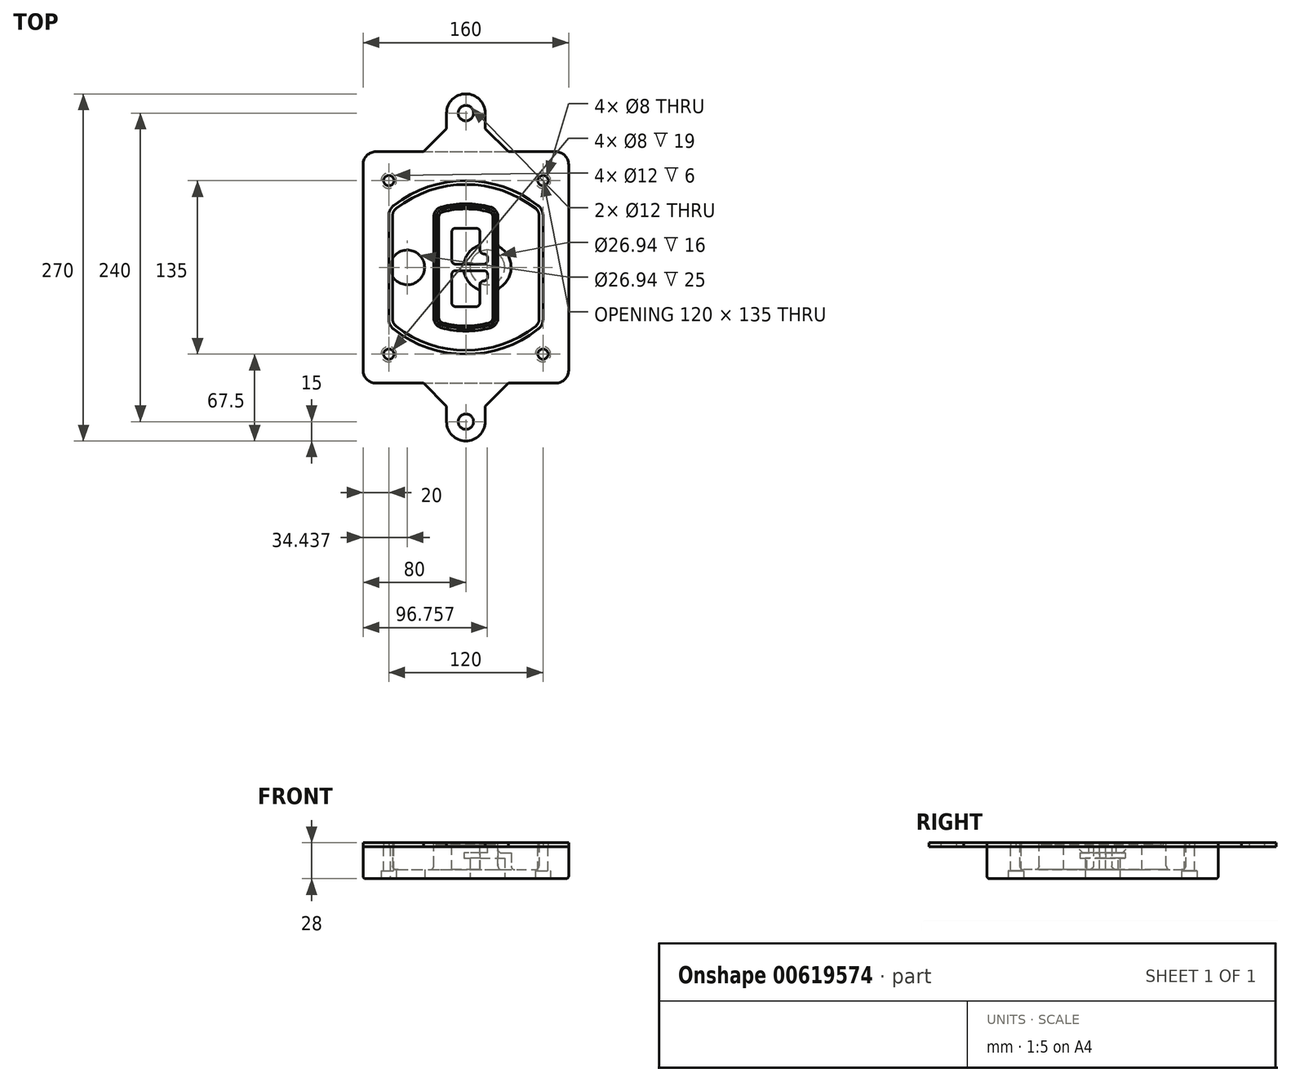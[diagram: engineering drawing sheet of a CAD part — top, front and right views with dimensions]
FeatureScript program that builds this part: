
annotation { "Feature Type Name" : "Feature", "Feature Type Description" : "" }
export const myFeature = defineFeature(function(context is Context, id is Id, definition is map)
    precondition{}
    {
        {
            var Q0;
            Q0=qCreatedBy(makeId("Top.planeOp"),FACE);
            var sketch = newSketch(context, id + "F0", { "sketchPlane" : qUnion([Q0])});
            skPoint(sketch, "E0.rect.middle", {"position": v(0, 0) * mm});
            skLineSegment(sketch, "E1.bottom", {"start": v(-70, -90) * mm, "end": v(70, -90) * mm});
            skLineSegment(sketch, "E1.top", {"start": v(-70, 90) * mm, "end": v(70, 90) * mm});
            skLineSegment(sketch, "E1.left", {"start": v(-80, -80) * mm, "end": v(-80, 80) * mm});
            skLineSegment(sketch, "E1.right", {"start": v(80, -80) * mm, "end": v(80, 80) * mm});
            skLineSegment(sketch, "E2", {"start": v(-80, 90) * mm, "end": v(80, -90) * mm, "construction": true});
            skLineSegment(sketch, "E3", {"start": v(80, 90) * mm, "end": v(-80, -90) * mm, "construction": true});
            skCircle(sketch, "E4", {"center": v(-60, 67.5) * mm, "radius": 4 * mm});
            skCircle(sketch, "E5", {"center": v(60, 67.5) * mm, "radius": 4 * mm});
            skCircle(sketch, "E6", {"center": v(60, -67.5) * mm, "radius": 4 * mm});
            skCircle(sketch, "E7", {"center": v(-60, -67.5) * mm, "radius": 4 * mm});
            skLineSegment(sketch, "E8", {"start": v(-60, 67.5) * mm, "end": v(60, 67.5) * mm, "construction": true});
            skLineSegment(sketch, "E9", {"start": v(60, 67.5) * mm, "end": v(60, -67.5) * mm, "construction": true});
            skLineSegment(sketch, "E10", {"start": v(60, -67.5) * mm, "end": v(-60, -67.5) * mm, "construction": true});
            skLineSegment(sketch, "E11", {"start": v(-60, -67.5) * mm, "end": v(-60, 67.5) * mm, "construction": true});
            skLineSegment(sketch, "E12", {"start": v(-60, 40.3) * mm, "end": v(-60, -40.3) * mm});
            skLineSegment(sketch, "E13", {"start": v(60, 40.3) * mm, "end": v(60, -40.3) * mm});
            skArc(sketch, "E14", {"start": v(56.15, 48.18) * mm, "mid": v(0, 67.5) * mm, "end": v(-56.15, 48.18) * mm});
            skArc(sketch, "E15", {"start": v(-56.15, -48.18) * mm, "mid": v(0, -67.5) * mm, "end": v(56.15, -48.18) * mm});
            skLineSegment(sketch, "E16", {"start": v(-60, 0) * mm, "end": v(60, 0) * mm, "construction": true});
            skPoint(sketch, "E17.visualSharp", {"position": v(-60, -45) * mm});
            skArc(sketch, "E17.filletArc", {"start": v(-60, -40.3) * mm, "mid": v(-58.99, -44.68) * mm, "end": v(-56.15, -48.18) * mm});
            skPoint(sketch, "E18.visualSharp", {"position": v(-60, 45) * mm});
            skArc(sketch, "E18.filletArc", {"start": v(-56.15, 48.18) * mm, "mid": v(-58.99, 44.68) * mm, "end": v(-60, 40.3) * mm});
            skPoint(sketch, "E19.visualSharp", {"position": v(60, 45) * mm});
            skArc(sketch, "E19.filletArc", {"start": v(60, 40.3) * mm, "mid": v(58.99, 44.68) * mm, "end": v(56.15, 48.18) * mm});
            skPoint(sketch, "E20.visualSharp", {"position": v(60, -45) * mm});
            skArc(sketch, "E20.filletArc", {"start": v(56.15, -48.18) * mm, "mid": v(58.99, -44.68) * mm, "end": v(60, -40.3) * mm});
            skPoint(sketch, "E21.visualSharp", {"position": v(-80, 90) * mm});
            skArc(sketch, "E21.filletArc", {"start": v(-70, 90) * mm, "mid": v(-77.07, 87.07) * mm, "end": v(-80, 80) * mm});
            skPoint(sketch, "E22.visualSharp", {"position": v(80, 90) * mm});
            skArc(sketch, "E22.filletArc", {"start": v(80, 80) * mm, "mid": v(77.07, 87.07) * mm, "end": v(70, 90) * mm});
            skPoint(sketch, "E23.visualSharp", {"position": v(80, -90) * mm});
            skArc(sketch, "E23.filletArc", {"start": v(70, -90) * mm, "mid": v(77.07, -87.07) * mm, "end": v(80, -80) * mm});
            skPoint(sketch, "E24.visualSharp", {"position": v(-80, -90) * mm});
            skArc(sketch, "E24.filletArc", {"start": v(-80, -80) * mm, "mid": v(-77.07, -87.07) * mm, "end": v(-70, -90) * mm});
            skArc(sketch, "E25.0", {"start": v(57, 40.3) * mm, "mid": v(56.3, 43.36) * mm, "end": v(54.3, 45.81) * mm});
            skLineSegment(sketch, "E25.1", {"start": v(57, 40.3) * mm, "end": v(57, -40.3) * mm});
            skArc(sketch, "E25.2", {"start": v(54.3, -45.81) * mm, "mid": v(56.3, -43.36) * mm, "end": v(57, -40.3) * mm});
            skArc(sketch, "E25.3", {"start": v(-54.3, -45.81) * mm, "mid": v(0, -64.5) * mm, "end": v(54.3, -45.81) * mm});
            skArc(sketch, "E25.4", {"start": v(-57, -40.3) * mm, "mid": v(-56.3, -43.36) * mm, "end": v(-54.3, -45.81) * mm});
            skArc(sketch, "E25.5", {"start": v(54.3, 45.81) * mm, "mid": v(0, 64.5) * mm, "end": v(-54.3, 45.81) * mm});
            skLineSegment(sketch, "E25.6", {"start": v(-57, 40.3) * mm, "end": v(-57, -40.3) * mm});
            skArc(sketch, "E25.7", {"start": v(-54.3, 45.81) * mm, "mid": v(-56.3, 43.36) * mm, "end": v(-57, 40.3) * mm});
            skArc(sketch, "E26.0", {"start": v(-58.62, 51.33) * mm, "mid": v(-62.58, 46.43) * mm, "end": v(-64, 40.3) * mm});
            skArc(sketch, "E26.1", {"start": v(58.62, 51.33) * mm, "mid": v(0, 71.5) * mm, "end": v(-58.62, 51.33) * mm});
            skArc(sketch, "E26.2", {"start": v(64, 40.3) * mm, "mid": v(62.58, 46.43) * mm, "end": v(58.62, 51.33) * mm});
            skLineSegment(sketch, "E26.3", {"start": v(64, 40.3) * mm, "end": v(64, -40.3) * mm});
            skArc(sketch, "E26.4", {"start": v(58.62, -51.33) * mm, "mid": v(62.58, -46.43) * mm, "end": v(64, -40.3) * mm});
            skLineSegment(sketch, "E26.5", {"start": v(-64, 40.3) * mm, "end": v(-64, -40.3) * mm});
            skArc(sketch, "E26.6", {"start": v(-58.62, -51.33) * mm, "mid": v(0, -71.5) * mm, "end": v(58.62, -51.33) * mm});
            skArc(sketch, "E26.7", {"start": v(-64, -40.3) * mm, "mid": v(-62.58, -46.43) * mm, "end": v(-58.62, -51.33) * mm});
            skSolve(sketch);
        }
        {
            var Q0;
            Q0=makeQuery(id+"F0.imprint","IMPRINT",FACE,{"disambiguationData":[TD([[makeQuery(id+"F0.imprint","IMPRINT",EDGE,{"derivedFrom":sQuery(id+"F0.wireOp",EDGE,"E1.bottom")}),1.0]])]});
            var Q1;
            Q1=makeQuery(id+"F0.imprint","IMPRINT",FACE,{"disambiguationData":[TD([[makeQuery(id+"F0.imprint","IMPRINT",EDGE,{"derivedFrom":sQuery(id+"F0.wireOp",EDGE,"E12")}),1.0]])]});
            var Q2;
            Q2=makeQuery(id+"F0.imprint","IMPRINT",FACE,{"disambiguationData":[TD([[makeQuery(id+"F0.imprint","IMPRINT",EDGE,{"derivedFrom":sQuery(id+"F0.wireOp",EDGE,"E25.0")}),1.0]])]});
            var Q3;
            Q3=makeQuery(id+"F0.imprint","IMPRINT",FACE,{"disambiguationData":[TD([[makeQuery(id+"F0.imprint","IMPRINT",EDGE,{"derivedFrom":sQuery(id+"F0.wireOp",EDGE,"E12")}),-1.0]])]});
            extrude(context, id + "F1", {"entities" : qUnion([Q0, Q1, Q2, Q3]), "oppositeDirection" : true, "depth" : 25 * mm});
        }
        {
            var Q0;
            Q0=makeQuery(id+"F0.imprint","IMPRINT",FACE,{"disambiguationData":[TD([[makeQuery(id+"F0.imprint","IMPRINT",EDGE,{"derivedFrom":sQuery(id+"F0.wireOp",EDGE,"E12")}),1.0]])]});
            extrude(context, id + "F2", {"entities" : qUnion([Q0]), "operationType" : NewBodyOperationType.ADD, "depth" : 3 * mm});
        }
        {
            var Q0;
            Q0=makeQuery(id+"F0.imprint","IMPRINT",FACE,{"disambiguationData":[TD([[makeQuery(id+"F0.imprint","IMPRINT",EDGE,{"derivedFrom":sQuery(id+"F0.wireOp",EDGE,"E25.0")}),1.0]])]});
            extrude(context, id + "F3", {"entities" : qUnion([Q0]), "operationType" : NewBodyOperationType.REMOVE, "oppositeDirection" : true, "depth" : 18 * mm});
        }
        {
            var Q0;
            Q0=makeQuery(id+"F2.opExtrude","CAP_FACE",FACE,{"disambiguationData":[OSD([sQuery(id+"F0.wireOp",EDGE,"E12"),sQuery(id+"F0.wireOp",EDGE,"E13"),sQuery(id+"F0.wireOp",EDGE,"E14"),sQuery(id+"F0.wireOp",EDGE,"E15"),sQuery(id+"F0.wireOp",EDGE,"E17.filletArc"),sQuery(id+"F0.wireOp",EDGE,"E18.filletArc"),sQuery(id+"F0.wireOp",EDGE,"E19.filletArc"),sQuery(id+"F0.wireOp",EDGE,"E20.filletArc"),sQuery(id+"F0.wireOp",EDGE,"E25.0"),sQuery(id+"F0.wireOp",EDGE,"E25.1"),sQuery(id+"F0.wireOp",EDGE,"E25.2"),sQuery(id+"F0.wireOp",EDGE,"E25.3"),sQuery(id+"F0.wireOp",EDGE,"E25.4"),sQuery(id+"F0.wireOp",EDGE,"E25.5"),sQuery(id+"F0.wireOp",EDGE,"E25.6"),sQuery(id+"F0.wireOp",EDGE,"E25.7")])],"isStart":false});
            var sketch = newSketch(context, id + "F4", { "sketchPlane" : qUnion([Q0])});
            skArc(sketch, "E27.0", {"start": v(-19.08, -46.97) * mm, "mid": v(0, -49.5) * mm, "end": v(19.08, -46.97) * mm});
            skArc(sketch, "E28.0", {"start": v(19.08, 46.97) * mm, "mid": v(0, 49.5) * mm, "end": v(-19.08, 46.97) * mm});
            skLineSegment(sketch, "E29", {"start": v(-25, 39.25) * mm, "end": v(-25, -39.25) * mm});
            skLineSegment(sketch, "E30", {"start": v(25, 39.25) * mm, "end": v(25, -39.25) * mm});
            skLineSegment(sketch, "E31", {"start": v(-25, 45.1) * mm, "end": v(25, 45.1) * mm, "construction": true});
            skLineSegment(sketch, "E32", {"start": v(-25, -45.1) * mm, "end": v(25, -45.1) * mm, "construction": true});
            skPoint(sketch, "E33.visualSharp", {"position": v(-25, 45.1) * mm});
            skArc(sketch, "E33.filletArc", {"start": v(-19.08, 46.97) * mm, "mid": v(-23.35, 44.11) * mm, "end": v(-25, 39.25) * mm});
            skPoint(sketch, "E34.visualSharp", {"position": v(25, 45.1) * mm});
            skArc(sketch, "E34.filletArc", {"start": v(25, 39.25) * mm, "mid": v(23.35, 44.11) * mm, "end": v(19.08, 46.97) * mm});
            skPoint(sketch, "E35.visualSharp", {"position": v(25, -45.1) * mm});
            skArc(sketch, "E35.filletArc", {"start": v(19.08, -46.97) * mm, "mid": v(23.35, -44.11) * mm, "end": v(25, -39.25) * mm});
            skPoint(sketch, "E36.visualSharp", {"position": v(-25, -45.1) * mm});
            skArc(sketch, "E36.filletArc", {"start": v(-25, -39.25) * mm, "mid": v(-23.35, -44.11) * mm, "end": v(-19.08, -46.97) * mm});
            skArc(sketch, "E37.0", {"start": v(54.3, 45.81) * mm, "mid": v(0, 64.5) * mm, "end": v(-54.3, 45.81) * mm});
            skArc(sketch, "E37.1", {"start": v(-54.3, 45.81) * mm, "mid": v(-56.3, 43.36) * mm, "end": v(-57, 40.3) * mm});
            skLineSegment(sketch, "E37.2", {"start": v(-57, 40.3) * mm, "end": v(-57, -40.3) * mm});
            skArc(sketch, "E37.3", {"start": v(-57, -40.3) * mm, "mid": v(-56.3, -43.36) * mm, "end": v(-54.3, -45.81) * mm});
            skArc(sketch, "E37.4", {"start": v(-54.3, -45.81) * mm, "mid": v(0, -64.5) * mm, "end": v(54.3, -45.81) * mm});
            skArc(sketch, "E37.5", {"start": v(54.3, -45.81) * mm, "mid": v(56.3, -43.36) * mm, "end": v(57, -40.3) * mm});
            skLineSegment(sketch, "E37.6", {"start": v(57, 40.3) * mm, "end": v(57, -40.3) * mm});
            skArc(sketch, "E37.7", {"start": v(57, 40.3) * mm, "mid": v(56.3, 43.36) * mm, "end": v(54.3, 45.81) * mm});
            skLineSegment(sketch, "E38.0", {"start": v(23, 39.25) * mm, "end": v(23, -39.25) * mm});
            skArc(sketch, "E38.1", {"start": v(18.56, -45.04) * mm, "mid": v(21.76, -42.9) * mm, "end": v(23, -39.25) * mm});
            skArc(sketch, "E38.2", {"start": v(-18.56, -45.04) * mm, "mid": v(0, -47.5) * mm, "end": v(18.56, -45.04) * mm});
            skArc(sketch, "E38.3", {"start": v(-23, -39.25) * mm, "mid": v(-21.76, -42.9) * mm, "end": v(-18.56, -45.04) * mm});
            skLineSegment(sketch, "E38.4", {"start": v(-23, 39.25) * mm, "end": v(-23, -39.25) * mm});
            skArc(sketch, "E38.5", {"start": v(23, 39.25) * mm, "mid": v(21.76, 42.9) * mm, "end": v(18.56, 45.04) * mm});
            skArc(sketch, "E38.6", {"start": v(-18.56, 45.04) * mm, "mid": v(-21.76, 42.9) * mm, "end": v(-23, 39.25) * mm});
            skArc(sketch, "E38.7", {"start": v(18.56, 45.04) * mm, "mid": v(0, 47.5) * mm, "end": v(-18.56, 45.04) * mm});
            skArc(sketch, "E39.0", {"start": v(21, 39.25) * mm, "mid": v(20.18, 41.68) * mm, "end": v(18.04, 43.1) * mm});
            skLineSegment(sketch, "E39.1", {"start": v(21, 39.25) * mm, "end": v(21, -39.25) * mm});
            skArc(sketch, "E39.2", {"start": v(18.04, -43.1) * mm, "mid": v(20.18, -41.68) * mm, "end": v(21, -39.25) * mm});
            skArc(sketch, "E39.3", {"start": v(-18.04, -43.1) * mm, "mid": v(0, -45.5) * mm, "end": v(18.04, -43.1) * mm});
            skArc(sketch, "E39.4", {"start": v(-21, -39.25) * mm, "mid": v(-20.18, -41.68) * mm, "end": v(-18.04, -43.1) * mm});
            skArc(sketch, "E39.5", {"start": v(18.04, 43.1) * mm, "mid": v(0, 45.5) * mm, "end": v(-18.04, 43.1) * mm});
            skLineSegment(sketch, "E39.6", {"start": v(-21, 39.25) * mm, "end": v(-21, -39.25) * mm});
            skArc(sketch, "E39.7", {"start": v(-18.04, 43.1) * mm, "mid": v(-20.18, 41.68) * mm, "end": v(-21, 39.25) * mm});
            skLineSegment(sketch, "E40", {"start": v(-25, 0) * mm, "end": v(25, 0) * mm, "construction": true});
            skLineSegment(sketch, "E41", {"start": v(-11, 5.5) * mm, "end": v(-11, 27.5) * mm});
            skLineSegment(sketch, "E42", {"start": v(-8, 30.5) * mm, "end": v(8, 30.5) * mm});
            skLineSegment(sketch, "E43", {"start": v(11, 27.5) * mm, "end": v(11, 13.5) * mm});
            skLineSegment(sketch, "E44", {"start": v(14, 10.5) * mm, "end": v(14, 10.5) * mm});
            skLineSegment(sketch, "E45", {"start": v(17, 7.5) * mm, "end": v(17, 5.5) * mm});
            skLineSegment(sketch, "E46", {"start": v(14, 2.5) * mm, "end": v(-8, 2.5) * mm});
            skPoint(sketch, "E47.visualSharp", {"position": v(-11, 30.5) * mm});
            skArc(sketch, "E47.filletArc", {"start": v(-8, 30.5) * mm, "mid": v(-10.12, 29.62) * mm, "end": v(-11, 27.5) * mm});
            skPoint(sketch, "E48.visualSharp", {"position": v(11, 30.5) * mm});
            skArc(sketch, "E48.filletArc", {"start": v(11, 27.5) * mm, "mid": v(10.12, 29.62) * mm, "end": v(8, 30.5) * mm});
            skPoint(sketch, "E49.visualSharp", {"position": v(11, 10.5) * mm});
            skArc(sketch, "E49.filletArc", {"start": v(11, 13.5) * mm, "mid": v(11.88, 11.38) * mm, "end": v(14, 10.5) * mm});
            skPoint(sketch, "E50.visualSharp", {"position": v(17, 10.5) * mm});
            skArc(sketch, "E50.filletArc", {"start": v(17, 7.5) * mm, "mid": v(16.12, 9.62) * mm, "end": v(14, 10.5) * mm});
            skPoint(sketch, "E51.visualSharp", {"position": v(17, 2.5) * mm});
            skArc(sketch, "E51.filletArc", {"start": v(14, 2.5) * mm, "mid": v(16.12, 3.38) * mm, "end": v(17, 5.5) * mm});
            skPoint(sketch, "E52.visualSharp", {"position": v(-11, 2.5) * mm});
            skArc(sketch, "E52.filletArc", {"start": v(-11, 5.5) * mm, "mid": v(-10.12, 3.38) * mm, "end": v(-8, 2.5) * mm});
            skLineSegment(sketch, "E53.0.MirrorCS", {"start": v(14, -2.5) * mm, "end": v(-8, -2.5) * mm});
            skArc(sketch, "E54.0.MirrorCS", {"start": v(-11, -5.5) * mm, "mid": v(-10.12, -3.38) * mm, "end": v(-8, -2.5) * mm});
            skLineSegment(sketch, "E55.0.MirrorCS", {"start": v(-11, -5.5) * mm, "end": v(-11, -27.5) * mm});
            skArc(sketch, "E56.0.MirrorCS", {"start": v(-8, -30.5) * mm, "mid": v(-10.12, -29.62) * mm, "end": v(-11, -27.5) * mm});
            skLineSegment(sketch, "E57.0.MirrorCS", {"start": v(-8, -30.5) * mm, "end": v(8, -30.5) * mm});
            skArc(sketch, "E58.0.MirrorCS", {"start": v(11, -27.5) * mm, "mid": v(10.12, -29.62) * mm, "end": v(8, -30.5) * mm});
            skLineSegment(sketch, "E59.0.MirrorCS", {"start": v(11, -27.5) * mm, "end": v(11, -13.5) * mm});
            skArc(sketch, "E60.0.MirrorCS", {"start": v(11, -13.5) * mm, "mid": v(11.88, -11.38) * mm, "end": v(14, -10.5) * mm});
            skArc(sketch, "E61.0.MirrorCS", {"start": v(17, -7.5) * mm, "mid": v(16.12, -9.62) * mm, "end": v(14, -10.5) * mm});
            skLineSegment(sketch, "E62.0.MirrorCS", {"start": v(17, -7.5) * mm, "end": v(17, -5.5) * mm});
            skArc(sketch, "E63.0.MirrorCS", {"start": v(14, -2.5) * mm, "mid": v(16.12, -3.38) * mm, "end": v(17, -5.5) * mm});
            skSolve(sketch);
        }
        {
            var Q0;
            Q0=makeQuery(id+"F4.imprint","IMPRINT",FACE,{"disambiguationData":[TD([[makeQuery(id+"F4.imprint","IMPRINT",EDGE,{"derivedFrom":sQuery(id+"F4.wireOp",EDGE,"E27.0")}),1.0]])]});
            var Q1;
            Q1=makeQuery(id+"F4.imprint","IMPRINT",FACE,{"disambiguationData":[TD([[makeQuery(id+"F4.imprint","IMPRINT",EDGE,{"derivedFrom":sQuery(id+"F4.wireOp",EDGE,"E38.0")}),-1.0]])]});
            var Q2;
            Q2=makeQuery(id+"F4.imprint","IMPRINT",FACE,{"disambiguationData":[TD([[makeQuery(id+"F4.imprint","IMPRINT",EDGE,{"derivedFrom":sQuery(id+"F4.wireOp",EDGE,"E39.0")}),1.0]])]});
            extrude(context, id + "F5", {"entities" : qUnion([Q0, Q1, Q2]), "operationType" : NewBodyOperationType.ADD, "endBound" : BoundingType.UP_TO_NEXT, "oppositeDirection" : true, "depth" : 25 * mm});
        }
        {
            var Q0;
            Q0=makeQuery(id+"F4.imprint","IMPRINT",FACE,{"disambiguationData":[TD([[makeQuery(id+"F4.imprint","IMPRINT",EDGE,{"derivedFrom":sQuery(id+"F4.wireOp",EDGE,"E38.0")}),-1.0]])]});
            extrude(context, id + "F6", {"entities" : qUnion([Q0]), "operationType" : NewBodyOperationType.REMOVE, "oppositeDirection" : true, "depth" : 2 * mm});
        }
        {
            var Q0;
            Q0=makeQuery(id+"F1.opExtrude","CAP_FACE",FACE,{"disambiguationData":[OSD([sQuery(id+"F0.wireOp",EDGE,"E1.bottom"),sQuery(id+"F0.wireOp",EDGE,"E1.top"),sQuery(id+"F0.wireOp",EDGE,"E1.left"),sQuery(id+"F0.wireOp",EDGE,"E1.right"),sQuery(id+"F0.wireOp",EDGE,"E4"),sQuery(id+"F0.wireOp",EDGE,"E5"),sQuery(id+"F0.wireOp",EDGE,"E6"),sQuery(id+"F0.wireOp",EDGE,"E7"),sQuery(id+"F0.wireOp",EDGE,"E21.filletArc"),sQuery(id+"F0.wireOp",EDGE,"E22.filletArc"),sQuery(id+"F0.wireOp",EDGE,"E23.filletArc"),sQuery(id+"F0.wireOp",EDGE,"E24.filletArc")])],"isStart":false});
            var sketch = newSketch(context, id + "F7", { "sketchPlane" : qUnion([Q0])});
            skCircle(sketch, "E64", {"center": v(16.76, 0) * mm, "radius": 13.47 * mm});
            skCircle(sketch, "E65", {"center": v(-45.56, 0) * mm, "radius": 13.47 * mm});
            skLineSegment(sketch, "E66", {"start": v(80, 0) * mm, "end": v(-80, 0) * mm});
            skCircle(sketch, "E67", {"center": v(16.76, 0) * mm, "radius": 18.47 * mm});
            skCircle(sketch, "E68", {"center": v(60, -67.5) * mm, "radius": 6 * mm});
            skCircle(sketch, "E69", {"center": v(-60, -67.5) * mm, "radius": 6 * mm});
            skCircle(sketch, "E70", {"center": v(-60, 67.5) * mm, "radius": 6 * mm});
            skCircle(sketch, "E71", {"center": v(60, 67.5) * mm, "radius": 6 * mm});
            skSolve(sketch);
        }
        {
            var Q0;
            {var subQ1=sQuery(id+"F7.wireOp",EDGE,"E66");var subQ4=sQuery(id+"F7.wireOp",EDGE,"E64");var subQ6=makeQuery(id+"F7.imprint","INTERSECT",VERTEX,{"disambiguationData":[OD(0.0)],"derivedFrom":[subQ4,subQ1]});Q0=makeQuery(id+"F7.imprint","IMPRINT",FACE,{"disambiguationData":[TD([[makeQuery(id+"F7.imprint","IMPRINT",EDGE,{"disambiguationData":[TD([[subQ6,-1.0]])],"derivedFrom":subQ4}),-1.0]])]});}
            var Q1;
            {var subQ0=sQuery(id+"F7.wireOp",EDGE,"E66");var subQ1=sQuery(id+"F7.wireOp",EDGE,"E64");var subQ3=makeQuery(id+"F7.imprint","INTERSECT",VERTEX,{"disambiguationData":[OD(0.0)],"derivedFrom":[subQ1,subQ0]});Q1=makeQuery(id+"F7.imprint","IMPRINT",FACE,{"disambiguationData":[TD([[makeQuery(id+"F7.imprint","IMPRINT",EDGE,{"disambiguationData":[TD([[subQ3,-1.0]])],"derivedFrom":subQ1}),1.0]])]});}
            var Q2;
            {var subQ0=sQuery(id+"F7.wireOp",EDGE,"E66");var subQ1=sQuery(id+"F7.wireOp",EDGE,"E64");var subQ3=makeQuery(id+"F7.imprint","INTERSECT",VERTEX,{"disambiguationData":[OD(0.0)],"derivedFrom":[subQ1,subQ0]});Q2=makeQuery(id+"F7.imprint","IMPRINT",FACE,{"disambiguationData":[TD([[makeQuery(id+"F7.imprint","IMPRINT",EDGE,{"disambiguationData":[TD([[subQ3,1.0]])],"derivedFrom":subQ1}),1.0]])]});}
            var Q3;
            {var subQ1=sQuery(id+"F7.wireOp",EDGE,"E66");var subQ4=sQuery(id+"F7.wireOp",EDGE,"E64");var subQ6=makeQuery(id+"F7.imprint","INTERSECT",VERTEX,{"disambiguationData":[OD(0.0)],"derivedFrom":[subQ4,subQ1]});Q3=makeQuery(id+"F7.imprint","IMPRINT",FACE,{"disambiguationData":[TD([[makeQuery(id+"F7.imprint","IMPRINT",EDGE,{"disambiguationData":[TD([[subQ6,1.0]])],"derivedFrom":subQ4}),-1.0]])]});}
            extrude(context, id + "F8", {"entities" : qUnion([Q0, Q1, Q2, Q3]), "operationType" : NewBodyOperationType.ADD, "oppositeDirection" : true, "depth" : 20 * mm});
        }
        {
            var Q0;
            {var subQ0=sQuery(id+"F7.wireOp",EDGE,"E66");var subQ1=sQuery(id+"F7.wireOp",EDGE,"E64");var subQ3=makeQuery(id+"F7.imprint","INTERSECT",VERTEX,{"disambiguationData":[OD(0.0)],"derivedFrom":[subQ1,subQ0]});Q0=makeQuery(id+"F7.imprint","IMPRINT",FACE,{"disambiguationData":[TD([[makeQuery(id+"F7.imprint","IMPRINT",EDGE,{"disambiguationData":[TD([[subQ3,-1.0]])],"derivedFrom":subQ1}),1.0]])]});}
            var Q1;
            {var subQ0=sQuery(id+"F7.wireOp",EDGE,"E66");var subQ1=sQuery(id+"F7.wireOp",EDGE,"E64");var subQ3=makeQuery(id+"F7.imprint","INTERSECT",VERTEX,{"disambiguationData":[OD(0.0)],"derivedFrom":[subQ1,subQ0]});Q1=makeQuery(id+"F7.imprint","IMPRINT",FACE,{"disambiguationData":[TD([[makeQuery(id+"F7.imprint","IMPRINT",EDGE,{"disambiguationData":[TD([[subQ3,1.0]])],"derivedFrom":subQ1}),1.0]])]});}
            extrude(context, id + "F9", {"entities" : qUnion([Q0, Q1]), "operationType" : NewBodyOperationType.REMOVE, "oppositeDirection" : true, "depth" : 16 * mm});
        }
        {
            var Q0;
            {var subQ0=sQuery(id+"F7.wireOp",EDGE,"E66");var subQ1=sQuery(id+"F7.wireOp",EDGE,"E65");var subQ3=makeQuery(id+"F7.imprint","INTERSECT",VERTEX,{"disambiguationData":[OD(0.0)],"derivedFrom":[subQ1,subQ0]});Q0=makeQuery(id+"F7.imprint","IMPRINT",FACE,{"disambiguationData":[TD([[makeQuery(id+"F7.imprint","IMPRINT",EDGE,{"disambiguationData":[TD([[subQ3,-1.0]])],"derivedFrom":subQ1}),1.0]])]});}
            var Q1;
            {var subQ0=sQuery(id+"F7.wireOp",EDGE,"E66");var subQ1=sQuery(id+"F7.wireOp",EDGE,"E65");var subQ3=makeQuery(id+"F7.imprint","INTERSECT",VERTEX,{"disambiguationData":[OD(0.0)],"derivedFrom":[subQ1,subQ0]});Q1=makeQuery(id+"F7.imprint","IMPRINT",FACE,{"disambiguationData":[TD([[makeQuery(id+"F7.imprint","IMPRINT",EDGE,{"disambiguationData":[TD([[subQ3,1.0]])],"derivedFrom":subQ1}),1.0]])]});}
            extrude(context, id + "F10", {"entities" : qUnion([Q0, Q1]), "operationType" : NewBodyOperationType.REMOVE, "oppositeDirection" : true, "depth" : 25 * mm});
        }
        {
            var Q0;
            Q0=makeQuery(id+"F7.imprint","IMPRINT",FACE,{"disambiguationData":[TD([[makeQuery(id+"F7.imprint","IMPRINT",EDGE,{"derivedFrom":sQuery(id+"F7.wireOp",EDGE,"E68")}),1.0]])]});
            var Q1;
            Q1=makeQuery(id+"F7.imprint","IMPRINT",FACE,{"disambiguationData":[TD([[makeQuery(id+"F7.imprint","IMPRINT",EDGE,{"derivedFrom":makeQuery(id+"F1.opExtrude","CAP_EDGE",EDGE,{"disambiguationData":[OSD([sQuery(id+"F0.wireOp",EDGE,"E5")])],"isStart":false})}),-1.0]])]});
            var Q2;
            Q2=makeQuery(id+"F7.imprint","IMPRINT",FACE,{"disambiguationData":[TD([[makeQuery(id+"F7.imprint","IMPRINT",EDGE,{"derivedFrom":sQuery(id+"F7.wireOp",EDGE,"E69")}),1.0]])]});
            var Q3;
            Q3=makeQuery(id+"F7.imprint","IMPRINT",FACE,{"disambiguationData":[TD([[makeQuery(id+"F7.imprint","IMPRINT",EDGE,{"derivedFrom":makeQuery(id+"F1.opExtrude","CAP_EDGE",EDGE,{"disambiguationData":[OSD([sQuery(id+"F0.wireOp",EDGE,"E4")])],"isStart":false})}),-1.0]])]});
            var Q4;
            Q4=makeQuery(id+"F7.imprint","IMPRINT",FACE,{"disambiguationData":[TD([[makeQuery(id+"F7.imprint","IMPRINT",EDGE,{"derivedFrom":sQuery(id+"F7.wireOp",EDGE,"E70")}),1.0]])]});
            var Q5;
            Q5=makeQuery(id+"F7.imprint","IMPRINT",FACE,{"disambiguationData":[TD([[makeQuery(id+"F7.imprint","IMPRINT",EDGE,{"derivedFrom":makeQuery(id+"F1.opExtrude","CAP_EDGE",EDGE,{"disambiguationData":[OSD([sQuery(id+"F0.wireOp",EDGE,"E7")])],"isStart":false})}),-1.0]])]});
            var Q6;
            Q6=makeQuery(id+"F7.imprint","IMPRINT",FACE,{"disambiguationData":[TD([[makeQuery(id+"F7.imprint","IMPRINT",EDGE,{"derivedFrom":sQuery(id+"F7.wireOp",EDGE,"E71")}),1.0]])]});
            var Q7;
            Q7=makeQuery(id+"F7.imprint","IMPRINT",FACE,{"disambiguationData":[TD([[makeQuery(id+"F7.imprint","IMPRINT",EDGE,{"derivedFrom":makeQuery(id+"F1.opExtrude","CAP_EDGE",EDGE,{"disambiguationData":[OSD([sQuery(id+"F0.wireOp",EDGE,"E6")])],"isStart":false})}),-1.0]])]});
            extrude(context, id + "F11", {"entities" : qUnion([Q0, Q1, Q2, Q3, Q4, Q5, Q6, Q7]), "operationType" : NewBodyOperationType.REMOVE, "oppositeDirection" : true, "depth" : 6 * mm});
        }
        {
            var Q0;
            Q0=makeQuery(id+"F9.boolean.opBoolean","COPY",FACE,{"derivedFrom":makeQuery(id+"F9.opExtrude","CAP_FACE",FACE,{"disambiguationData":[OSD([sQuery(id+"F7.wireOp",EDGE,"E64")])],"isStart":false})});
            var sketch = newSketch(context, id + "F12", { "sketchPlane" : qUnion([Q0])});
            skArc(sketch, "E72.0", {"start": v(11, 17.55) * mm, "mid": v(2.57, 11.82) * mm, "end": v(-1.54, 2.5) * mm});
            skArc(sketch, "E72.1", {"start": v(-1.54, -2.5) * mm, "mid": v(2.57, -11.82) * mm, "end": v(11, -17.55) * mm});
            skLineSegment(sketch, "E73", {"start": v(-1.54, -2.5) * mm, "end": v(14, -2.5) * mm});
            skLineSegment(sketch, "E74.0", {"start": v(14, 2.5) * mm, "end": v(-1.54, 2.5) * mm});
            skArc(sketch, "E74.1", {"start": v(14, 2.5) * mm, "mid": v(16.12, 3.38) * mm, "end": v(17, 5.5) * mm});
            skLineSegment(sketch, "E74.2", {"start": v(17, 7.5) * mm, "end": v(17, 5.5) * mm});
            skArc(sketch, "E74.3", {"start": v(17, 7.5) * mm, "mid": v(16.12, 9.62) * mm, "end": v(14, 10.5) * mm});
            skArc(sketch, "E74.4", {"start": v(11, 13.5) * mm, "mid": v(11.88, 11.38) * mm, "end": v(14, 10.5) * mm});
            skLineSegment(sketch, "E74.5", {"start": v(11, 17.55) * mm, "end": v(11, 13.5) * mm});
            skLineSegment(sketch, "E74.7", {"start": v(14, -2.5) * mm, "end": v(-1.54, -2.5) * mm});
            skArc(sketch, "E74.8", {"start": v(14, -2.5) * mm, "mid": v(16.12, -3.38) * mm, "end": v(17, -5.5) * mm});
            skLineSegment(sketch, "E74.9", {"start": v(17, -7.5) * mm, "end": v(17, -5.5) * mm});
            skArc(sketch, "E74.10", {"start": v(17, -7.5) * mm, "mid": v(16.12, -9.62) * mm, "end": v(14, -10.5) * mm});
            skArc(sketch, "E74.11", {"start": v(11, -13.5) * mm, "mid": v(11.88, -11.38) * mm, "end": v(14, -10.5) * mm});
            skLineSegment(sketch, "E74.12", {"start": v(11, -17.55) * mm, "end": v(11, -13.5) * mm});
            skPoint(sketch, "E75.orphan", {"position": v(11, -27.5) * mm});
            skPoint(sketch, "E76.orphan", {"position": v(-8, -2.5) * mm});
            skPoint(sketch, "E77.orphan", {"position": v(-8, 2.5) * mm});
            skPoint(sketch, "E78.orphan", {"position": v(11, 27.5) * mm});
            skSolve(sketch);
        }
        {
            var Q0;
            {var subQ7=sQuery(id+"F12.wireOp",EDGE,"E72.0");var subQ14=sQuery(id+"F12.wireOp",EDGE,"E72.1");var subQ16=sQuery(id+"F12.wireOp",EDGE,"E74.1");var subQ18=sQuery(id+"F12.wireOp",EDGE,"E74.8");Q0=qUnion([makeQuery(id+"F12.imprint","IMPRINT",FACE,{"disambiguationData":[TD([[makeQuery(id+"F12.imprint","IMPRINT",EDGE,{"derivedFrom":subQ7}),1.0]])]}),makeQuery(id+"F12.imprint","IMPRINT",FACE,{"disambiguationData":[TD([[makeQuery(id+"F12.imprint","IMPRINT",EDGE,{"derivedFrom":subQ14}),1.0]])]}),makeQuery(id+"F12.imprint","IMPRINT",FACE,{"disambiguationData":[TD([[makeQuery(id+"F12.imprint","IMPRINT",EDGE,{"derivedFrom":subQ16}),1.0]])]}),makeQuery(id+"F12.imprint","IMPRINT",FACE,{"disambiguationData":[TD([[makeQuery(id+"F12.imprint","IMPRINT",EDGE,{"derivedFrom":subQ18}),-1.0]])]})]);}
            var Q1;
            Q1=makeQuery(id+"F5.boolean.opBoolean","SPLIT",FACE,{"disambiguationData":[TD([makeQuery(id+"F5.opExtrude","SWEPT_FACE",FACE,{"disambiguationData":[OSD([sQuery(id+"F4.wireOp",EDGE,"E41")])]})])],"derivedFrom":makeQuery(id+"F3.boolean.opBoolean","COPY",FACE,{"derivedFrom":makeQuery(id+"F3.opExtrude","CAP_FACE",FACE,{"disambiguationData":[OSD([sQuery(id+"F0.wireOp",EDGE,"E25.0"),sQuery(id+"F0.wireOp",EDGE,"E25.1"),sQuery(id+"F0.wireOp",EDGE,"E25.2"),sQuery(id+"F0.wireOp",EDGE,"E25.3"),sQuery(id+"F0.wireOp",EDGE,"E25.4"),sQuery(id+"F0.wireOp",EDGE,"E25.5"),sQuery(id+"F0.wireOp",EDGE,"E25.6"),sQuery(id+"F0.wireOp",EDGE,"E25.7")])],"isStart":false})})});
            extrude(context, id + "F13", {"entities" : qUnion([Q0]), "operationType" : NewBodyOperationType.REMOVE, "endBound" : BoundingType.UP_TO_SURFACE, "endBoundEntityFace" : qUnion([Q1]), "depth" : 25 * mm});
        }
        {
            var Q0;
            Q0=makeQuery(id+"F3.boolean.opBoolean","COPY",EDGE,{"derivedFrom":makeQuery(id+"F3.opExtrude","CAP_EDGE",EDGE,{"disambiguationData":[OSD([sQuery(id+"F0.wireOp",EDGE,"E25.6")])],"isStart":false})});
            var Q1;
            Q1=makeQuery(id+"F8.boolean.opBoolean","INTERSECT",EDGE,{"derivedFrom":[makeQuery(id+"F5.opExtrude","SWEPT_FACE",FACE,{"disambiguationData":[OSD([sQuery(id+"F4.wireOp",EDGE,"E30")])]}),makeQuery(id+"F8.opExtrude","CAP_FACE",FACE,{"disambiguationData":[OSD([sQuery(id+"F7.wireOp",EDGE,"E67")])],"isStart":false})]});
            var Q2;
            Q2=makeQuery(id+"F8.boolean.opBoolean","INTERSECT",EDGE,{"disambiguationData":[OD(1.0)],"derivedFrom":[makeQuery(id+"F5.opExtrude","SWEPT_FACE",FACE,{"disambiguationData":[OSD([sQuery(id+"F4.wireOp",EDGE,"E30")])]}),makeQuery(id+"F8.opExtrude","SWEPT_FACE",FACE,{"disambiguationData":[OSD([sQuery(id+"F7.wireOp",EDGE,"E67")])]})]});
            var Q3;
            {var subQ0=sQuery(id+"F4.wireOp",EDGE,"E30");Q3=makeQuery(id+"F8.boolean.opBoolean","SPLIT",EDGE,{"disambiguationData":[TD([makeQuery(id+"F5.opExtrude","SWEPT_FACE",FACE,{"disambiguationData":[OSD([sQuery(id+"F4.wireOp",EDGE,"E35.filletArc")])]})])],"derivedFrom":makeQuery(id+"F5.opExtrude","CAP_EDGE",EDGE,{"disambiguationData":[OSD([subQ0])],"isStart":false})});}
            var Q4;
            {var subQ0=sQuery(id+"F0.wireOp",EDGE,"E25.7");var subQ1=sQuery(id+"F0.wireOp",EDGE,"E25.1");var subQ2=sQuery(id+"F0.wireOp",EDGE,"E25.6");var subQ3=sQuery(id+"F0.wireOp",EDGE,"E25.5");var subQ4=sQuery(id+"F0.wireOp",EDGE,"E25.4");var subQ5=sQuery(id+"F0.wireOp",EDGE,"E25.0");var subQ6=sQuery(id+"F0.wireOp",EDGE,"E25.2");var subQ7=sQuery(id+"F0.wireOp",EDGE,"E25.3");Q4=makeQuery(id+"F8.boolean.opBoolean","INTERSECT",EDGE,{"derivedFrom":[makeQuery(id+"F5.boolean.opBoolean","SPLIT",FACE,{"disambiguationData":[TD([makeQuery(id+"F2.opExtrude","SWEPT_FACE",FACE,{"disambiguationData":[OSD([subQ5])]})])],"derivedFrom":makeQuery(id+"F3.boolean.opBoolean","COPY",FACE,{"derivedFrom":makeQuery(id+"F3.opExtrude","CAP_FACE",FACE,{"disambiguationData":[OSD([subQ5,subQ1,subQ6,subQ7,subQ4,subQ3,subQ2,subQ0])],"isStart":false})})}),makeQuery(id+"F8.opExtrude","SWEPT_FACE",FACE,{"disambiguationData":[OSD([sQuery(id+"F7.wireOp",EDGE,"E67")])]})]});}
            var Q5;
            Q5=makeQuery(id+"F8.boolean.opBoolean","INTERSECT",EDGE,{"disambiguationData":[OD(0.0)],"derivedFrom":[makeQuery(id+"F5.opExtrude","SWEPT_FACE",FACE,{"disambiguationData":[OSD([sQuery(id+"F4.wireOp",EDGE,"E30")])]}),makeQuery(id+"F8.opExtrude","SWEPT_FACE",FACE,{"disambiguationData":[OSD([sQuery(id+"F7.wireOp",EDGE,"E67")])]})]});
            fillet(context, id + "F14", {"entities" : qUnion([Q0, Q1, Q2, Q3, Q4, Q5]), "radius" : 3 * mm, "tangentPropagation" : true, "allowEdgeOverflow" : false});
        }
        {
            var Q0;
            Q0=makeQuery(id+"F1.opExtrude","CAP_EDGE",EDGE,{"disambiguationData":[OSD([sQuery(id+"F0.wireOp",EDGE,"E1.bottom")])],"isStart":false});
            fillet(context, id + "F15", {"entities" : qUnion([Q0]), "radius" : 2 * mm, "tangentPropagation" : true, "allowEdgeOverflow" : false});
        }
        {
            var Q0;
            {var subQ0=sQuery(id+"F0.wireOp",EDGE,"E21.filletArc");var subQ1=sQuery(id+"F0.wireOp",EDGE,"E7");var subQ2=sQuery(id+"F0.wireOp",EDGE,"E6");var subQ3=sQuery(id+"F0.wireOp",EDGE,"E5");var subQ4=sQuery(id+"F0.wireOp",EDGE,"E4");var subQ5=sQuery(id+"F0.wireOp",EDGE,"E22.filletArc");var subQ6=sQuery(id+"F0.wireOp",EDGE,"E1.bottom");var subQ7=sQuery(id+"F0.wireOp",EDGE,"E1.right");var subQ8=sQuery(id+"F0.wireOp",EDGE,"E1.top");var subQ9=sQuery(id+"F0.wireOp",EDGE,"E1.left");var subQ10=sQuery(id+"F0.wireOp",EDGE,"E23.filletArc");var subQ11=sQuery(id+"F0.wireOp",EDGE,"E24.filletArc");Q0=makeQuery(id+"F2.boolean.opBoolean","SPLIT",FACE,{"disambiguationData":[TD([makeQuery(id+"F1.opExtrude","SWEPT_FACE",FACE,{"disambiguationData":[OSD([subQ6])]})])],"derivedFrom":makeQuery(id+"F1.opExtrude","CAP_FACE",FACE,{"disambiguationData":[OSD([subQ6,subQ8,subQ9,subQ7,subQ4,subQ3,subQ2,subQ1,subQ0,subQ5,subQ10,subQ11])],"isStart":true})});}
            var sketch = newSketch(context, id + "F16", { "sketchPlane" : qUnion([Q0])});
            skLineSegment(sketch, "E79.0", {"start": v(-70, 90) * mm, "end": v(70, 90) * mm});
            skArc(sketch, "E79.1", {"start": v(-70, 90) * mm, "mid": v(-77.07, 87.07) * mm, "end": v(-80, 80) * mm});
            skLineSegment(sketch, "E79.2", {"start": v(-80, -80) * mm, "end": v(-80, 80) * mm});
            skLineSegment(sketch, "E79.3", {"start": v(80, -80) * mm, "end": v(80, 80) * mm});
            skArc(sketch, "E79.4", {"start": v(80, 80) * mm, "mid": v(77.07, 87.07) * mm, "end": v(70, 90) * mm});
            skArc(sketch, "E79.5", {"start": v(70, -90) * mm, "mid": v(77.07, -87.07) * mm, "end": v(80, -80) * mm});
            skLineSegment(sketch, "E79.6", {"start": v(-70, -90) * mm, "end": v(70, -90) * mm});
            skArc(sketch, "E79.7", {"start": v(-80, -80) * mm, "mid": v(-77.07, -87.07) * mm, "end": v(-70, -90) * mm});
            skArc(sketch, "E79.8", {"start": v(-56.15, -48.18) * mm, "mid": v(0, -67.5) * mm, "end": v(56.15, -48.18) * mm});
            skArc(sketch, "E79.9", {"start": v(-60, -40.3) * mm, "mid": v(-58.99, -44.68) * mm, "end": v(-56.15, -48.18) * mm});
            skLineSegment(sketch, "E79.10", {"start": v(-60, 40.3) * mm, "end": v(-60, -40.3) * mm});
            skArc(sketch, "E79.11", {"start": v(56.15, 48.18) * mm, "mid": v(0, 67.5) * mm, "end": v(-56.15, 48.18) * mm});
            skArc(sketch, "E79.12", {"start": v(-56.15, 48.18) * mm, "mid": v(-58.99, 44.68) * mm, "end": v(-60, 40.3) * mm});
            skLineSegment(sketch, "E79.13", {"start": v(60, 40.3) * mm, "end": v(60, -40.3) * mm});
            skArc(sketch, "E79.14", {"start": v(60, 40.3) * mm, "mid": v(58.99, 44.68) * mm, "end": v(56.15, 48.18) * mm});
            skArc(sketch, "E79.15", {"start": v(56.15, -48.18) * mm, "mid": v(58.99, -44.68) * mm, "end": v(60, -40.3) * mm});
            skCircle(sketch, "E80.0", {"center": v(-60, 67.5) * mm, "radius": 4 * mm});
            skCircle(sketch, "E80.1", {"center": v(60, 67.5) * mm, "radius": 4 * mm});
            skCircle(sketch, "E80.2", {"center": v(-60, -67.5) * mm, "radius": 4 * mm});
            skCircle(sketch, "E80.3", {"center": v(60, -67.5) * mm, "radius": 4 * mm});
            skLineSegment(sketch, "E81", {"start": v(0, 90) * mm, "end": v(0, 120) * mm, "construction": true});
            skPoint(sketch, "E81.endSnap0", {"position": v(0, 90) * mm});
            skCircle(sketch, "E82", {"center": v(0, 120) * mm, "radius": 6 * mm});
            skLineSegment(sketch, "E83", {"start": v(-33, 90) * mm, "end": v(-15, 108) * mm});
            skLineSegment(sketch, "E84", {"start": v(-15, 108) * mm, "end": v(-15, 120) * mm});
            skLineSegment(sketch, "E85", {"start": v(33, 90) * mm, "end": v(15, 108) * mm});
            skLineSegment(sketch, "E86", {"start": v(15, 108) * mm, "end": v(15, 120) * mm});
            skArc(sketch, "E87", {"start": v(15, 120) * mm, "mid": v(0, 135) * mm, "end": v(-15, 120) * mm});
            skLineSegment(sketch, "E88", {"start": v(-80, 0) * mm, "end": v(80, 0) * mm, "construction": true});
            skLineSegment(sketch, "E89.MirrorCS", {"start": v(0, -90) * mm, "end": v(0, -120) * mm, "construction": true});
            skArc(sketch, "E90.MirrorCS", {"start": v(15, -120) * mm, "mid": v(0, -135) * mm, "end": v(-15, -120) * mm});
            skLineSegment(sketch, "E91.MirrorCS", {"start": v(15, -108) * mm, "end": v(15, -120) * mm});
            skCircle(sketch, "E92.MirrorC", {"center": v(0, -120) * mm, "radius": 6 * mm});
            skLineSegment(sketch, "E93.MirrorCS", {"start": v(-15, -108) * mm, "end": v(-15, -120) * mm});
            skPoint(sketch, "E94.MirrorP", {"position": v(0, -90) * mm});
            skLineSegment(sketch, "E95.MirrorCS", {"start": v(33, -90) * mm, "end": v(15, -108) * mm});
            skLineSegment(sketch, "E96.MirrorCS", {"start": v(-33, -90) * mm, "end": v(-15, -108) * mm});
            skSolve(sketch);
        }
        {
            var Q0;
            Q0 = qSketchRegion(id + "F16", true);
            var Q1;
            Q1=makeQuery(id+"F2.opExtrude","CAP_FACE",FACE,{"disambiguationData":[OSD([sQuery(id+"F0.wireOp",EDGE,"E12"),sQuery(id+"F0.wireOp",EDGE,"E13"),sQuery(id+"F0.wireOp",EDGE,"E14"),sQuery(id+"F0.wireOp",EDGE,"E15"),sQuery(id+"F0.wireOp",EDGE,"E17.filletArc"),sQuery(id+"F0.wireOp",EDGE,"E18.filletArc"),sQuery(id+"F0.wireOp",EDGE,"E19.filletArc"),sQuery(id+"F0.wireOp",EDGE,"E20.filletArc"),sQuery(id+"F0.wireOp",EDGE,"E25.0"),sQuery(id+"F0.wireOp",EDGE,"E25.1"),sQuery(id+"F0.wireOp",EDGE,"E25.2"),sQuery(id+"F0.wireOp",EDGE,"E25.3"),sQuery(id+"F0.wireOp",EDGE,"E25.4"),sQuery(id+"F0.wireOp",EDGE,"E25.5"),sQuery(id+"F0.wireOp",EDGE,"E25.6"),sQuery(id+"F0.wireOp",EDGE,"E25.7")])],"isStart":false});
            extrude(context, id + "F17", {"entities" : qUnion([Q0]), "endBound" : BoundingType.UP_TO_SURFACE, "depth" : 25 * mm, "endBoundEntityFace" : qUnion([Q1]), "offsetDistance" : 25 * mm});
        }
    });
